# Revit family: Hager-Golf-IP40-Transparent_Door-sistema-PT-pt
name_source: partatom
category: Electrical Equipment
units: mm (PartAtom-declared; Revit-internal decimal feet)

## family parameters
Cut with Voids When Loaded = No
Host = Face
Panel Configuration = Two Columns, Circuits Across
Part Type = Panelboard
Room Calculation Point = No
Round Connector Dimension = Use Diameter
Shared = No

## types (22) — shared parameters
EF000007 - Cor = EV000202 - Branco
EF000116 - Número RAL = 9010
EF000118 - Com tampa de montagem = No
EF000339 - Tipo de difusor = EV004216 - Porta
EF001062 - Versão EMC = No
EF001088 - Extensão possível = Yes
EF001134 - Calha DIN = Yes
EF001596 - Material do corpo = EV000139 - Plástico
EF004462 - Tipo de fecho = EV000154 - Outro
EF006244 - Tampa/porta transparente = Yes
EF006306 - Com fecho = No
EF009212 - Tipo de tampa = EV000116 - Fechado
EF015776 - Borne de terra = Yes
EF015777 - Borne de neutro = Yes
EF015941 - Porta para passagem de sinal = Yes
HG000001 - Número de colunas = 1
HG000002 - Com porta ou tampa = Yes
HG000003 - Gama = Golf
HG000005 - Espessura = 3 mm  [stored 0.00984252 ft]
HG000009 - Porta dupla = No
HG000010 - Portas assimétricas = No
HG000011 - Filas vazias desde da parte de baixo = No
HG000017 - Distância entre polos = 18 mm  [stored 0.0590551 ft]
Manufacturer = Hager
Type Comments = Golf
zero-valued in all types: Default Elevation, HG000007 - Número de colunas vazias, HG000008 - Número de filas vazias

## per-type parameters (varying)
| type | EF000003 - Método de montagem | EF000008 - Largura | EF000040 - Altura | EF000049 - Profundidade | EF000218 - Profundidade incorporada | EF000266 - Número de linhas | EF000332 - Altura embutida | EF000846 - Largura para embutir | EF001131 - Profundidade interior | EF002950 - Largura em número de módulos | EF005474 - Grau de proteção (IP) | HG000004 - Referência do Fabricante | HG000006 - Encastrado | Model |
| Montagem em superfície  L138 A184 P99 4 unidade de divisão - VS104TP | EV000384 - Montagem em superfície (gesso) | 138 mm  [stored 0.452756 ft] | 184 mm  [stored 0.603675 ft] | 99 mm  [stored 0.324803 ft] | 0 mm  [stored 0 ft] | 1 | 0 mm  [stored 0 ft] | 0 mm  [stored 0 ft] | 99 mm  [stored 0.324803 ft] | 4 |  | VS104TP | No | VS104TP |
| Montagem em superfície  L210 A184 P99 8 unidade de divisão - VS108TP | EV000384 - Montagem em superfície (gesso) | 210 mm  [stored 0.688976 ft] | 184 mm  [stored 0.603675 ft] | 99 mm  [stored 0.324803 ft] | 0 mm  [stored 0 ft] | 1 | 0 mm  [stored 0 ft] | 0 mm  [stored 0 ft] | 99 mm  [stored 0.324803 ft] | 8 |  | VS108TP | No | VS108TP |
| Montagem em superfície IP40 L282 A252 P99 12 unidade de divisão - VS112TP | EV000384 - Montagem em superfície (gesso) | 282 mm | 252 mm  [stored 0.826772 ft] | 99 mm  [stored 0.324803 ft] | 0 mm  [stored 0 ft] | 1 | 0 mm  [stored 0 ft] | 0 mm  [stored 0 ft] | 99 mm  [stored 0.324803 ft] | 12 | EV006415 - IP40 | VS112TP | No | VS112TP |
| Montagem em superfície IP40 L282 A377 P99 12 unidade de divisão - VS212TP | EV000384 - Montagem em superfície (gesso) | 282 mm | 377 mm  [stored 1.23688 ft] | 99 mm  [stored 0.324803 ft] | 0 mm  [stored 0 ft] | 2 | 0 mm  [stored 0 ft] | 0 mm  [stored 0 ft] | 99 mm  [stored 0.324803 ft] | 12 | EV006415 - IP40 | VS212TP | No | VS212TP |
| Montagem em superfície IP40 L282 A500 P99 12 unidade de divisão - VS312TP | EV000384 - Montagem em superfície (gesso) | 282 mm | 500 mm  [stored 1.64042 ft] | 99 mm  [stored 0.324803 ft] | 0 mm  [stored 0 ft] | 3 | 0 mm  [stored 0 ft] | 0 mm  [stored 0 ft] | 99 mm  [stored 0.324803 ft] | 12 | EV006415 - IP40 | VS312TP | No | VS312TP |
| Montagem em superfície IP40 L282 A647 P99 12 unidade de divisão - VS412TP | EV000384 - Montagem em superfície (gesso) | 282 mm | 647 mm  [stored 2.1227 ft] | 99 mm  [stored 0.324803 ft] | 0 mm  [stored 0 ft] | 4 | 0 mm  [stored 0 ft] | 0 mm  [stored 0 ft] | 99 mm  [stored 0.324803 ft] | 12 | EV006415 - IP40 | VS412TP | No | VS412TP |
| Montagem em superfície IP40 L390 A252 P99 18 unidade de divisão - VS118TP | EV000384 - Montagem em superfície (gesso) | 390 mm  [stored 1.27953 ft] | 252 mm  [stored 0.826772 ft] | 99 mm  [stored 0.324803 ft] | 0 mm  [stored 0 ft] | 1 | 0 mm  [stored 0 ft] | 0 mm  [stored 0 ft] | 99 mm  [stored 0.324803 ft] | 18 | EV006415 - IP40 | VS118TP | No | VS118TP |
| Montagem em superfície IP40 L390 A377 P99 18 unidade de divisão - VS218TP | EV000384 - Montagem em superfície (gesso) | 390 mm  [stored 1.27953 ft] | 377 mm  [stored 1.23688 ft] | 99 mm  [stored 0.324803 ft] | 0 mm  [stored 0 ft] | 2 | 0 mm  [stored 0 ft] | 0 mm  [stored 0 ft] | 99 mm  [stored 0.324803 ft] | 18 | EV006415 - IP40 | VS218TP | No | VS218TP |
| Montagem em superfície IP40 L390 A500 P99 18 unidade de divisão - VS318TP | EV000384 - Montagem em superfície (gesso) | 390 mm  [stored 1.27953 ft] | 500 mm  [stored 1.64042 ft] | 99 mm  [stored 0.324803 ft] | 0 mm  [stored 0 ft] | 3 | 0 mm  [stored 0 ft] | 0 mm  [stored 0 ft] | 99 mm  [stored 0.324803 ft] | 18 | EV006415 - IP40 | VS318TP | No | VS318TP |
| Montagem em superfície IP40 L390 A647 P99 18 unidade de divisão - VS418TP | EV000384 - Montagem em superfície (gesso) | 390 mm  [stored 1.27953 ft] | 647 mm  [stored 2.1227 ft] | 99 mm  [stored 0.324803 ft] | 0 mm  [stored 0 ft] | 4 | 0 mm  [stored 0 ft] | 0 mm  [stored 0 ft] | 99 mm  [stored 0.324803 ft] | 18 | EV006415 - IP40 | VS418TP | No | VS418TP |
| Montagem em superfície IP40 L462 A252 P99 22 unidade de divisão - VS122TP | EV000384 - Montagem em superfície (gesso) | 462 mm  [stored 1.51575 ft] | 252 mm  [stored 0.826772 ft] | 99 mm  [stored 0.324803 ft] | 0 mm  [stored 0 ft] | 1 | 0 mm  [stored 0 ft] | 0 mm  [stored 0 ft] | 99 mm  [stored 0.324803 ft] | 22 | EV006415 - IP40 | VS122TP | No | VS122TP |
| Montagem embutida  L204 A225 P97.5 4 unidade de divisão - VF104TP | EV000383 - Montagem embutida (gesso) | 204 mm | 225 mm  [stored 0.738189 ft] | 98 mm  [stored 0.321522 ft] | 72 mm  [stored 0.23622 ft] | 1 | 189 mm  [stored 0.620079 ft] | 170 mm  [stored 0.557743 ft] | 98 mm  [stored 0.321522 ft] | 4 |  | VF104TP | Yes | VF104TP |
| Montagem embutida  L275 A225 P97.5 8 unidade de divisão - VF108TP | EV000383 - Montagem embutida (gesso) | 275 mm | 225 mm  [stored 0.738189 ft] | 98 mm  [stored 0.321522 ft] | 72 mm  [stored 0.23622 ft] | 1 | 189 mm  [stored 0.620079 ft] | 242 mm  [stored 0.793963 ft] | 98 mm  [stored 0.321522 ft] | 8 |  | VF108TP | Yes | VF108TP |
| Montagem embutida IP40 L352 A293 P97.5 12 unidade de divisão - VF112TP | EV000383 - Montagem embutida (gesso) | 352 mm  [stored 1.15486 ft] | 293 mm | 98 mm  [stored 0.321522 ft] | 72 mm  [stored 0.23622 ft] | 1 | 257 mm  [stored 0.843176 ft] | 318 mm  [stored 1.04331 ft] | 98 mm  [stored 0.321522 ft] | 12 | EV006415 - IP40 | VF112TP | Yes | VF112TP |
| Montagem embutida IP40 L352 A543 P97.5 12 unidade de divisão - VF312TP | EV000383 - Montagem embutida (gesso) | 352 mm  [stored 1.15486 ft] | 543 mm  [stored 1.7815 ft] | 98 mm  [stored 0.321522 ft] | 72 mm  [stored 0.23622 ft] | 3 | 507 mm  [stored 1.66339 ft] | 318 mm  [stored 1.04331 ft] | 98 mm  [stored 0.321522 ft] | 12 | EV006415 - IP40 | VF312TP | Yes | VF312TP |
| Montagem embutida IP40 L352 A688 P97.5 12 unidade de divisão - VF412TP | EV000383 - Montagem embutida (gesso) | 352 mm  [stored 1.15486 ft] | 688 mm  [stored 2.25722 ft] | 98 mm  [stored 0.321522 ft] | 72 mm  [stored 0.23622 ft] | 4 | 652 mm  [stored 2.13911 ft] | 318 mm  [stored 1.04331 ft] | 98 mm  [stored 0.321522 ft] | 12 | EV006415 - IP40 | VF412TP | Yes | VF412TP |
| Montagem embutida IP40 L382 A418 P97.5 12 unidade de divisão - VF212TP | EV000383 - Montagem embutida (gesso) | 382 mm  [stored 1.25328 ft] | 418 mm  [stored 1.37139 ft] | 98 mm  [stored 0.321522 ft] | 72 mm  [stored 0.23622 ft] | 2 | 382 mm  [stored 1.25328 ft] | 318 mm  [stored 1.04331 ft] | 98 mm  [stored 0.321522 ft] | 12 | EV006415 - IP40 | VF212TP | Yes | VF212TP |
| Montagem embutida IP40 L460 A293 P97.5 18 unidade de divisão - VF118TP | EV000383 - Montagem embutida (gesso) | 460 mm  [stored 1.50919 ft] | 293 mm | 98 mm  [stored 0.321522 ft] | 72 mm  [stored 0.23622 ft] | 1 | 257 mm  [stored 0.843176 ft] | 426 mm  [stored 1.39764 ft] | 98 mm  [stored 0.321522 ft] | 18 | EV006415 - IP40 | VF118TP | Yes | VF118TP |
| Montagem embutida IP40 L460 A418 P97.5 18 unidade de divisão - VF218TP | EV000383 - Montagem embutida (gesso) | 460 mm  [stored 1.50919 ft] | 418 mm  [stored 1.37139 ft] | 98 mm  [stored 0.321522 ft] | 72 mm  [stored 0.23622 ft] | 2 | 382 mm  [stored 1.25328 ft] | 426 mm  [stored 1.39764 ft] | 98 mm  [stored 0.321522 ft] | 18 | EV006415 - IP40 | VF218TP | Yes | VF218TP |
| Montagem embutida IP40 L460 A543 P97.5 18 unidade de divisão - VF318TP | EV000383 - Montagem embutida (gesso) | 460 mm  [stored 1.50919 ft] | 543 mm  [stored 1.7815 ft] | 98 mm  [stored 0.321522 ft] | 72 mm  [stored 0.23622 ft] | 3 | 507 mm  [stored 1.66339 ft] | 426 mm  [stored 1.39764 ft] | 98 mm  [stored 0.321522 ft] | 18 | EV006415 - IP40 | VF318TP | Yes | VF318TP |
| Montagem embutida IP40 L460 A688 P97.5 18 unidade de divisão - VF418TP | EV000383 - Montagem embutida (gesso) | 460 mm  [stored 1.50919 ft] | 688 mm  [stored 2.25722 ft] | 98 mm  [stored 0.321522 ft] | 72 mm  [stored 0.23622 ft] | 4 | 652 mm  [stored 2.13911 ft] | 426 mm  [stored 1.39764 ft] | 98 mm  [stored 0.321522 ft] | 18 | EV006415 - IP40 | VF418TP | Yes | VF418TP |
| Montagem embutida IP40 L532 A293 P97.5 22 unidade de divisão - VF122TP | EV000383 - Montagem embutida (gesso) | 532 mm  [stored 1.74541 ft] | 293 mm | 98 mm  [stored 0.321522 ft] | 72 mm  [stored 0.23622 ft] | 1 | 257 mm  [stored 0.843176 ft] | 498 mm  [stored 1.63386 ft] | 98 mm  [stored 0.321522 ft] | 22 | EV006415 - IP40 | VF122TP | Yes | VF122TP |

note: [stored X ft] marks values corroborated as IEEE doubles in the binary element streams (Revit-internal decimal feet)

## geometry (parser evidence)
native form markers: Sweep x17
no freeform markers — native parametric forms only
